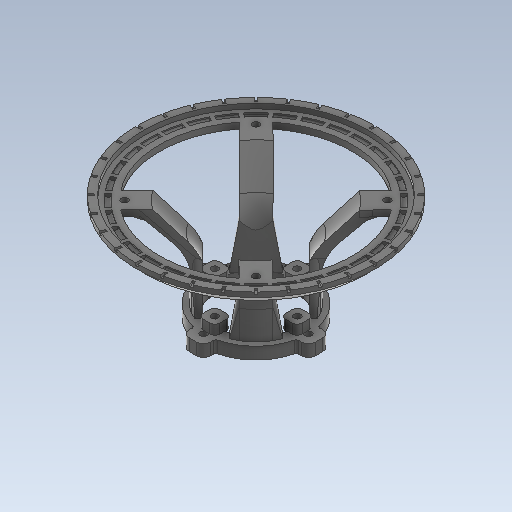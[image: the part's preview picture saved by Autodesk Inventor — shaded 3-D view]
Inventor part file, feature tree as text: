
AUTODESK INVENTOR PART (.ipt)
format: ipt  version: 2020 (Build 240168000, 168)  size: 1,987,072 bytes
history: native  units: mm
features: sketch x22, projected_geometry x22, other x20, extrude x10, revolve x9, pattern_circular x6, loft x5, fillet x4, chamfer x1, mirror x1
ambient origin geometry x8: Origin, YZ Plane, XZ Plane, XY Plane, X Axis, Y Axis, Z Axis, Center Point
bodies: Body1 (feature_tree)
feature tree (100):
  other  "Твердое тело1"
  extrude  "Выдавливание1"  Depth=34.0mm
  other  "РабПлоскость1"
  other  "РабОсь1"
  revolve  "Вращение1"
  sketch  "Эскиз3"
  other  "РабТочка1"
  extrude  "Выдавливание2"  Depth=45.0mm
  other  "РабТочка2"
  other  "РабТочка3"
  other  "РабТочка4"
  other  "РабПлоскость2"
  sketch  "Эскиз5"
  revolve  "Вращение2"
  revolve  "Вращение3"
  pattern_circular  "Круговой массив1"  Angle=45.0deg  [1 undecoded]
  extrude  "Выдавливание3"  Depth=2.9mm
  revolve  "Вращение4"
  sketch  "Эскиз8"
  fillet  "Сопряжение1"  Radius=9.0mm
  revolve  "Вращение5"
  other  "РабПлоскость6"
  other  "РабПлоскость7"
  sketch  "Эскиз10"
  revolve  "Вращение6"
  revolve  "Вращение7"
  sketch  "Эскиз11"
  sketch  "Эскиз12"
  loft  "Лофт2"
  loft  "Лофт3"
  fillet  "Сопряжение2"  Radius=1.0mm
  extrude  "Выдавливание4"  Depth=22.0mm
  loft  "Лофт4"
  fillet  "Сопряжение3"  Radius=5.0mm
  pattern_circular  "Круговой массив2"  [2 undecoded]
  revolve  "Вращение8"
  revolve  "Вращение9"
  extrude  "Выдавливание5"  Depth=2.5mm
  extrude  "Выдавливание6"  Depth=45.0mm
  pattern_circular  "Круговой массив3"  [2 undecoded]
  other  "РабПлоскость8"
  extrude  "Выдавливание8"  Depth=2.0mm
  extrude  "Выдавливание7"  Depth=2.0mm
  loft  "Лофт5"
  pattern_circular  "Круговой массив4"  Angle=45.0deg  [1 undecoded]
  fillet  "Сопряжение4"  [1 undecoded]
  chamfer  "Фаска1"  Distance=3.0mm
  sketch  "Эскиз23"
  extrude  "Выдавливание9"  TaperAngle=135.0deg  [1 undecoded]
  loft  "Лофт6"
  other  "РабПлоскость9"
  mirror  "Зеркальное отражение1"
  pattern_circular  "Круговой массив5"  [2 undecoded]
  extrude  "Выдавливание10"  TaperAngle=0.0deg  [1 undecoded]
  pattern_circular  "Круговой массив6"  [2 undecoded]
  sketch  "Эскиз1"
  sketch  "Эскиз2"
  sketch  "Эскиз4"
  projected_geometry  "Спроецированная петля1"
  projected_geometry  "Спроецированная петля2"
  projected_geometry  "Спроецированная петля3"
  other  "РабПлоскость3"
  other  "РабПлоскость4"
  other  "РабПлоскость5"
  sketch  "Эскиз6"
  sketch  "Эскиз7"
  sketch  "Эскиз9"
  projected_geometry  "Спроецированная петля4"
  projected_geometry  "Спроецированная петля5"
  other  "Ребра2"
  other  "Ребра3"
  other  "Ребра4"
  sketch  "Эскиз13"
  projected_geometry  "Спроецированная петля6"
  projected_geometry  "Спроецированная петля7"
  sketch  "Эскиз14"
  projected_geometry  "Спроецированная петля8"
  projected_geometry  "Спроецированная петля9"
  projected_geometry  "Спроецированная петля10"
  sketch  "Эскиз16"
  sketch  "Эскиз17"
  projected_geometry  "Спроецированная петля12"
  projected_geometry  "Спроецированная петля13"
  sketch  "Эскиз18"
  sketch  "Эскиз19"
  projected_geometry  "Спроецированная петля14"
  projected_geometry  "Спроецированная петля15"
  other  "Ребра5"
  sketch  "Эскиз22"
  projected_geometry  "Спроецированная петля16"
  projected_geometry  "Спроецированная петля17"
  projected_geometry  "Спроецированная петля18"
  projected_geometry  "Спроецированная петля19"
  projected_geometry  "Спроецированная петля20"
  sketch  "Эскиз24"
  other  "Ребра6"
  sketch  "Эскиз25"
  projected_geometry  "Спроецированная петля21"
  projected_geometry  "Спроецированная петля22"
  projected_geometry  "Спроецированная петля23"
note: 13 required parameter values undecoded (feature->parameter linkage not recoverable at this tier; creation-order binding heuristic only, values carry confidence <= 0.55)
